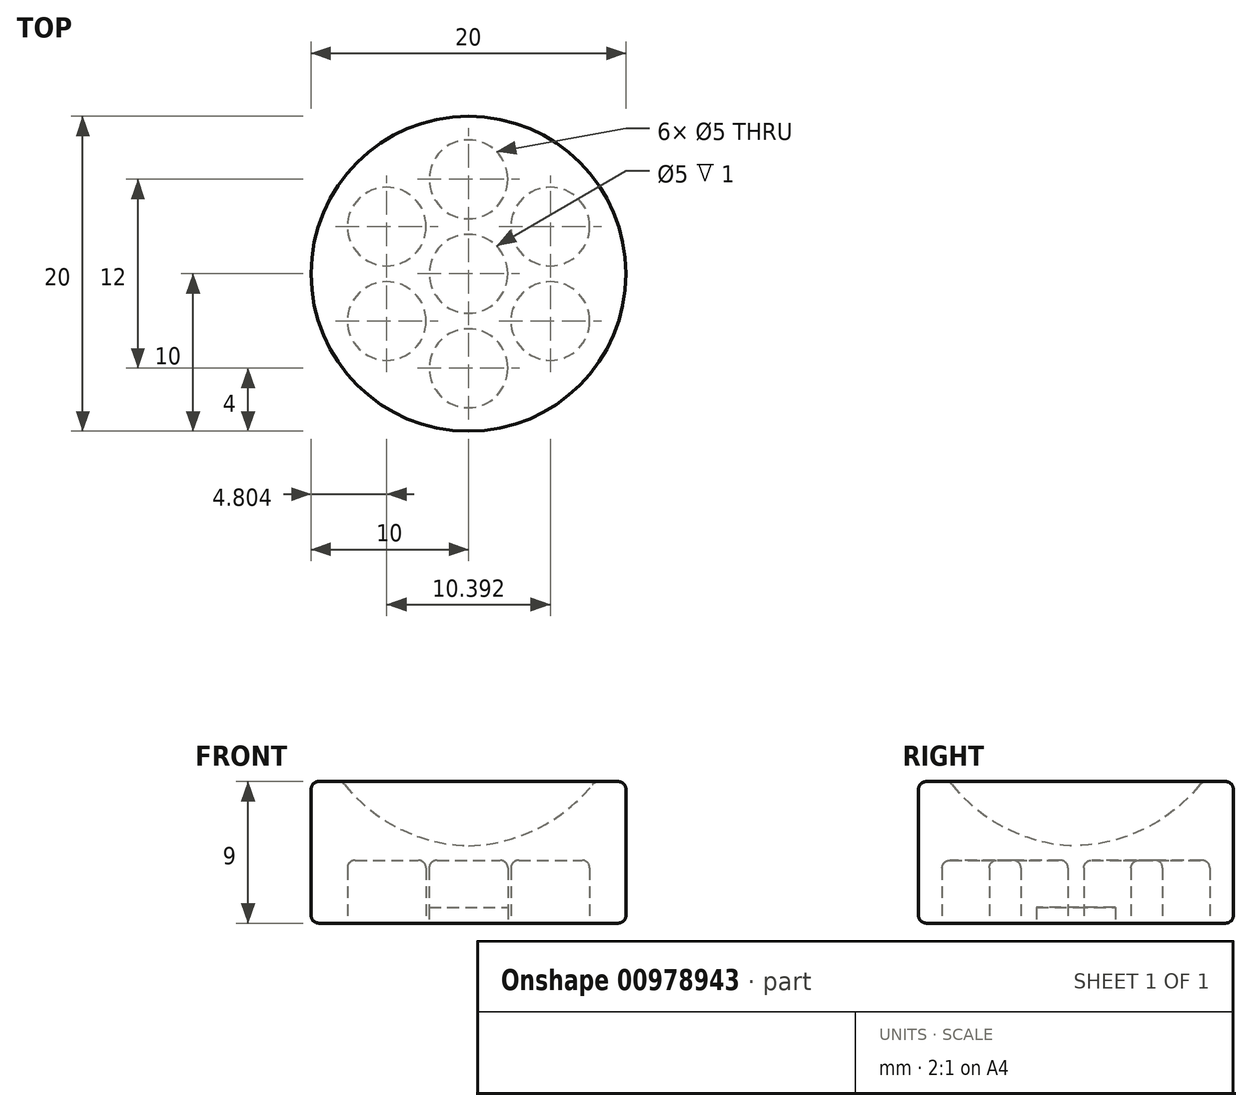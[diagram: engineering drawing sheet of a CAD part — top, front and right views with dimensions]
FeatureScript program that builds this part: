
annotation { "Feature Type Name" : "Feature", "Feature Type Description" : "" }
export const myFeature = defineFeature(function(context is Context, id is Id, definition is map)
    precondition{}
    {
        {
            var Q0;
            Q0=qCreatedBy(makeId("Front.planeOp"),FACE);
            var sketch = newSketch(context, id + "F0", { "sketchPlane" : qUnion([Q0])});
            skCircle(sketch, "E0", {"center": v(0, 0) * mm, "radius": 10 * mm, "construction": true});
            skLineSegment(sketch, "E1", {"start": v(8.03, -6) * mm, "end": v(10, -6) * mm});
            skLineSegment(sketch, "E2", {"start": v(10, -6) * mm, "end": v(10, -15) * mm});
            skLineSegment(sketch, "E3", {"start": v(10, -15) * mm, "end": v(0, -15) * mm});
            skLineSegment(sketch, "E4", {"start": v(0, -15) * mm, "end": v(0, -10.09) * mm});
            skLineSegment(sketch, "E5", {"start": v(-9.16, 13.08) * mm, "end": v(10.6, -15.15) * mm, "construction": true});
            skArc(sketch, "E6", {"start": v(0, -10.09) * mm, "mid": v(4.48, -8.95) * mm, "end": v(8.03, -6) * mm});
            skPoint(sketch, "E7.orphan", {"position": v(0, -10) * mm});
            skSolve(sketch);
        }
        {
            var Q0;
            {var subQ0=sQuery(id+"F0.wireOp",EDGE,"E1");Q0=makeQuery(id+"F0.imprint","IMPRINT",FACE,{"disambiguationData":[TD([[makeQuery(id+"F0.imprint","IMPRINT",EDGE,{"derivedFrom":subQ0}),-1.0]])]});}
            var Q1;
            Q1=sQuery(id+"F0.wireOp",EDGE,"E4");
            revolve(context, id + "F1", {"surfaceOperationType" : NewSurfaceOperationType.NEW, "entities" : qUnion([Q0]), "axis" : qUnion([Q1]), "revolveType" : RevolveType.FULL});
        }
        {
            var Q0;
            Q0=makeQuery(id+"F1.opRevolve","SWEPT_FACE",FACE,{"disambiguationData":[OSD([sQuery(id+"F0.wireOp",EDGE,"E3")])]});
            var sketch = newSketch(context, id + "F2", { "sketchPlane" : qUnion([Q0])});
            skCircle(sketch, "E8", {"center": v(0, 0) * mm, "radius": 2.5 * mm});
            skSolve(sketch);
        }
        {
            var Q0;
            Q0=makeQuery(id+"F2.imprint","IMPRINT",FACE,{"disambiguationData":[TD([[makeQuery(id+"F2.imprint","IMPRINT",EDGE,{"derivedFrom":sQuery(id+"F2.wireOp",EDGE,"E8")}),1.0]])]});
            extrude(context, id + "F3", {"entities" : qUnion([Q0]), "operationType" : NewBodyOperationType.REMOVE, "oppositeDirection" : true, "depth" : 1 * mm, "offsetDistance" : 25 * mm});
        }
        {
            var Q0;
            Q0=makeQuery(id+"F1.opRevolve","SWEPT_FACE",FACE,{"disambiguationData":[OSD([sQuery(id+"F0.wireOp",EDGE,"E3")])]});
            var sketch = newSketch(context, id + "F4", { "sketchPlane" : qUnion([Q0])});
            skCircle(sketch, "E9", {"center": v(0, 6) * mm, "radius": 2.5 * mm});
            skCircle(sketch, "E10.1.0", {"center": v(-5.2, 3) * mm, "radius": 2.5 * mm});
            skCircle(sketch, "E10.2.0", {"center": v(-5.2, -3) * mm, "radius": 2.5 * mm});
            skCircle(sketch, "E10.3.0", {"center": v(0, -6) * mm, "radius": 2.5 * mm});
            skCircle(sketch, "E10.4.0", {"center": v(5.2, -3) * mm, "radius": 2.5 * mm});
            skCircle(sketch, "E10.5.0", {"center": v(5.2, 3) * mm, "radius": 2.5 * mm});
            skPoint(sketch, "E10.center", {"position": v(0, 0) * mm});
            skSolve(sketch);
        }
        {
            var Q0;
            Q0=makeQuery(id+"F4.imprint","IMPRINT",FACE,{"disambiguationData":[TD([[makeQuery(id+"F4.imprint","IMPRINT",EDGE,{"derivedFrom":sQuery(id+"F4.wireOp",EDGE,"E10.1.0")}),1.0]])]});
            var Q1;
            Q1=makeQuery(id+"F4.imprint","IMPRINT",FACE,{"disambiguationData":[TD([[makeQuery(id+"F4.imprint","IMPRINT",EDGE,{"derivedFrom":sQuery(id+"F4.wireOp",EDGE,"E9")}),1.0]])]});
            var Q2;
            Q2=makeQuery(id+"F4.imprint","IMPRINT",FACE,{"disambiguationData":[TD([[makeQuery(id+"F4.imprint","IMPRINT",EDGE,{"derivedFrom":sQuery(id+"F4.wireOp",EDGE,"E10.5.0")}),1.0]])]});
            var Q3;
            Q3=makeQuery(id+"F4.imprint","IMPRINT",FACE,{"disambiguationData":[TD([[makeQuery(id+"F4.imprint","IMPRINT",EDGE,{"derivedFrom":sQuery(id+"F4.wireOp",EDGE,"E10.4.0")}),1.0]])]});
            var Q4;
            Q4=makeQuery(id+"F4.imprint","IMPRINT",FACE,{"disambiguationData":[TD([[makeQuery(id+"F4.imprint","IMPRINT",EDGE,{"derivedFrom":sQuery(id+"F4.wireOp",EDGE,"E10.3.0")}),1.0]])]});
            var Q5;
            Q5=makeQuery(id+"F4.imprint","IMPRINT",FACE,{"disambiguationData":[TD([[makeQuery(id+"F4.imprint","IMPRINT",EDGE,{"derivedFrom":sQuery(id+"F4.wireOp",EDGE,"E10.2.0")}),1.0]])]});
            extrude(context, id + "F5", {"entities" : qUnion([Q0, Q1, Q2, Q3, Q4, Q5]), "operationType" : NewBodyOperationType.REMOVE, "oppositeDirection" : true, "depth" : 4 * mm, "offsetDistance" : 25 * mm});
        }
        {
            var Q0;
            Q0=makeQuery(id+"F5.boolean.opBoolean","COPY",EDGE,{"derivedFrom":makeQuery(id+"F5.opExtrude","CAP_EDGE",EDGE,{"disambiguationData":[OSD([sQuery(id+"F4.wireOp",EDGE,"E10.4.0")])],"isStart":true})});
            var Q1;
            Q1=makeQuery(id+"F5.boolean.opBoolean","COPY",EDGE,{"derivedFrom":makeQuery(id+"F5.opExtrude","CAP_EDGE",EDGE,{"disambiguationData":[OSD([sQuery(id+"F4.wireOp",EDGE,"E10.3.0")])],"isStart":true})});
            var Q2;
            Q2=makeQuery(id+"F5.boolean.opBoolean","COPY",EDGE,{"derivedFrom":makeQuery(id+"F5.opExtrude","CAP_EDGE",EDGE,{"disambiguationData":[OSD([sQuery(id+"F4.wireOp",EDGE,"E10.2.0")])],"isStart":true})});
            var Q3;
            Q3=makeQuery(id+"F5.boolean.opBoolean","COPY",EDGE,{"derivedFrom":makeQuery(id+"F5.opExtrude","CAP_EDGE",EDGE,{"disambiguationData":[OSD([sQuery(id+"F4.wireOp",EDGE,"E10.1.0")])],"isStart":true})});
            var Q4;
            Q4=makeQuery(id+"F5.boolean.opBoolean","COPY",EDGE,{"derivedFrom":makeQuery(id+"F5.opExtrude","CAP_EDGE",EDGE,{"disambiguationData":[OSD([sQuery(id+"F4.wireOp",EDGE,"E9")])],"isStart":true})});
            var Q5;
            Q5=makeQuery(id+"F5.boolean.opBoolean","COPY",EDGE,{"derivedFrom":makeQuery(id+"F5.opExtrude","CAP_EDGE",EDGE,{"disambiguationData":[OSD([sQuery(id+"F4.wireOp",EDGE,"E10.5.0")])],"isStart":true})});
            var Q6;
            Q6=makeQuery(id+"F5.boolean.opBoolean","COPY",EDGE,{"derivedFrom":makeQuery(id+"F5.opExtrude","CAP_EDGE",EDGE,{"disambiguationData":[OSD([sQuery(id+"F4.wireOp",EDGE,"E10.4.0")])],"isStart":false})});
            var Q7;
            Q7=makeQuery(id+"F5.boolean.opBoolean","COPY",EDGE,{"derivedFrom":makeQuery(id+"F5.opExtrude","CAP_EDGE",EDGE,{"disambiguationData":[OSD([sQuery(id+"F4.wireOp",EDGE,"E10.3.0")])],"isStart":false})});
            var Q8;
            Q8=makeQuery(id+"F5.boolean.opBoolean","COPY",EDGE,{"derivedFrom":makeQuery(id+"F5.opExtrude","CAP_EDGE",EDGE,{"disambiguationData":[OSD([sQuery(id+"F4.wireOp",EDGE,"E10.2.0")])],"isStart":false})});
            var Q9;
            Q9=makeQuery(id+"F5.boolean.opBoolean","COPY",EDGE,{"derivedFrom":makeQuery(id+"F5.opExtrude","CAP_EDGE",EDGE,{"disambiguationData":[OSD([sQuery(id+"F4.wireOp",EDGE,"E10.1.0")])],"isStart":false})});
            var Q10;
            Q10=makeQuery(id+"F5.boolean.opBoolean","COPY",EDGE,{"derivedFrom":makeQuery(id+"F5.opExtrude","CAP_EDGE",EDGE,{"disambiguationData":[OSD([sQuery(id+"F4.wireOp",EDGE,"E9")])],"isStart":false})});
            var Q11;
            Q11=makeQuery(id+"F5.boolean.opBoolean","COPY",EDGE,{"derivedFrom":makeQuery(id+"F5.opExtrude","CAP_EDGE",EDGE,{"disambiguationData":[OSD([sQuery(id+"F4.wireOp",EDGE,"E10.5.0")])],"isStart":false})});
            fillet(context, id + "F6", {"entities" : qUnion([Q0, Q1, Q2, Q3, Q4, Q5, Q6, Q7, Q8, Q9, Q10, Q11]), "radius" : .5 * mm, "tangentPropagation" : true, "allowEdgeOverflow" : false});
        }
        {
            var Q0;
            Q0=makeQuery(id+"F1.opRevolve","SWEPT_EDGE",EDGE,{"disambiguationData":[OSD([sQuery(id+"F0.wireOp",EDGE,"E2"),sQuery(id+"F0.wireOp",EDGE,"E3")])]});
            var Q1;
            Q1=makeQuery(id+"F1.opRevolve","SWEPT_EDGE",EDGE,{"disambiguationData":[OSD([sQuery(id+"F0.wireOp",EDGE,"E1"),sQuery(id+"F0.wireOp",EDGE,"E2")])]});
            var Q2;
            Q2=makeQuery(id+"F1.opRevolve","SWEPT_EDGE",EDGE,{"disambiguationData":[OSD([sQuery(id+"F0.wireOp",EDGE,"E0"),sQuery(id+"F0.wireOp",EDGE,"E1")])]});
            fillet(context, id + "F7", {"entities" : qUnion([Q0, Q1, Q2]), "radius" : .5 * mm, "tangentPropagation" : true, "allowEdgeOverflow" : false});
        }
    });
